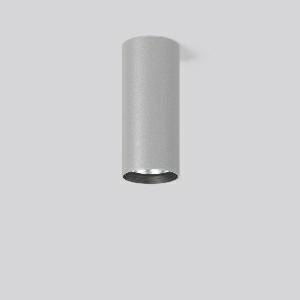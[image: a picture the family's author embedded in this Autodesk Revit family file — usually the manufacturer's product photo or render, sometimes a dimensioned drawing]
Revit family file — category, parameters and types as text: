
# Revit family: heledon_mini_a_931208_004_76_fef2
name_source: partatom
category: Lighting Fixtures
units: mm (PartAtom-declared; Revit-internal decimal feet)

## family parameters
Cut with Voids When Loaded = No
Host = Face
Light Source = No
Part Type = Normal
Room Calculation Point = No
Round Connector Dimension = Use Diameter
Shared = No

## types (1)
- HELEDON mini A (1 x LED Modul 930, 3550 lm, 3000)
    Apparent Load = 29 VA
    Approval mark = CE
    CIE Flux Codes = 100 100 100 100 100
    Color Rendering = 90
    Color Temperature = 3000
    Default Elevation = 1800 mm
    Description = Series: HELEDON mini
Cylindrical surface-mounted downlight. Housing: die-cast aluminium, powder-coated. Internal ceiling frame polycarbonate with bayonet mounting. Black plastic ring and recessed LED to prevent glare from the side. Optical assembly with reflector made of MIRO-Silver with 98% total light reflection for outstanding efficiency - can be changed without tools. Best colour rendering index Ra>90. Suitable for Ceiling mounting. Easy installation with a separate ceiling frame with bayonet mounting and plug connection. Driver integrated. Connected via plug-in connector. High quality converter without flickering and stroboscopic effect. The following accessories can be mounted without use of tools: interchangeable lenses, decorative glasses, honeycomb louvre, clear and frosted diffusers, white interchangeable plastic ring. 
Colour: silver
Diameter: 87 mm
Height: 197 mm
Lamp: LED
Socket: without socket
Colour temperature: 3000K
Colour rendering index (CRI): 92
System power: 29 W
Rated luminous flux: 3550 lm
Luminous efficiency: 122 lm/W
Control gear: Converter, dimmable, DALI
Protection class: I
Type of protection: IP 20
    Height = 197 mm
    Lamp = 1 x LED Modul 930
    Lamp Light Flux = 3550 lm
    Lamp count = 1
    Length = 87 mm
    Lifetime = 50000 h
    Luminous efficacy = 122 lm/W
    Manufacturer = RZB
    ModVariant = No
    Model = 931208.004.76
    Mounting Place = Ceiling
    Mounting Type = Surface mounted
    Number of Poles = 1
    OnlyDefault = Yes
    Power Factor = 1
    Product Name = HELEDON mini A
    Product group = Surface mounted downlights
    ProductGroupID = 302
    Protection Class = Protection class I
    Protection Degree = IP 20
    RLX_Detail_Level = 1
    RLX_Emergency_Light_Flux = 0 lm
    RLX_Emergency_Type = 0
    RLX_Emergency_Type_DB = No
    RlxData = <blob elided: 108265 chars, md5=e1363b1b>
    Socket = socket
    Standby Power = 0 W
    System Light Flux = 3550 lm
    System Power = 29 W
    Type Comments = Product without accessories
    Type Image = 931188.004.jpg
    URL = http://relux.com
    VarID = ---
    Voltage = 230 V
    Voltage Range = 220-240 V
    Weight = 0.00 kg
    Width = 0 mm  [stored 0 ft]

note: [stored X ft] marks values corroborated as IEEE doubles in the binary element streams (Revit-internal decimal feet)

## geometry (parser evidence)
native form markers: Blend x4, Sweep x10
no freeform markers — native parametric forms only
